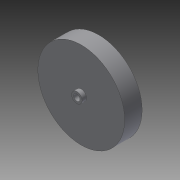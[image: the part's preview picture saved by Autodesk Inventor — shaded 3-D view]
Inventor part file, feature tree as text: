
AUTODESK INVENTOR PART (.ipt)
format: ipt  version: 2014 SP1 (Build 180222100, 222)  size: 81,408 bytes
history: native  units: in
note: dims shown in document units (in); Inventor stores cm internally (conversion verified against a paired STEP export)
features: extrude x2, sketch x1
ambient origin geometry x8: Origin, YZ Plane, XZ Plane, XY Plane, X Axis, Y Axis, Z Axis, Center Point
bodies: Solid1 (feature_tree)
feature tree (3):
  sketch  "Sketch1"  dims[d0=4.125in d1=0.3in d2=0.5in d3=0.83in d4=0.0in d5=1.25in d6=0.0in]
  extrude  "Extrusion1"  Depth=1.25in
  extrude  "Extrusion2"  Depth=1.25in
